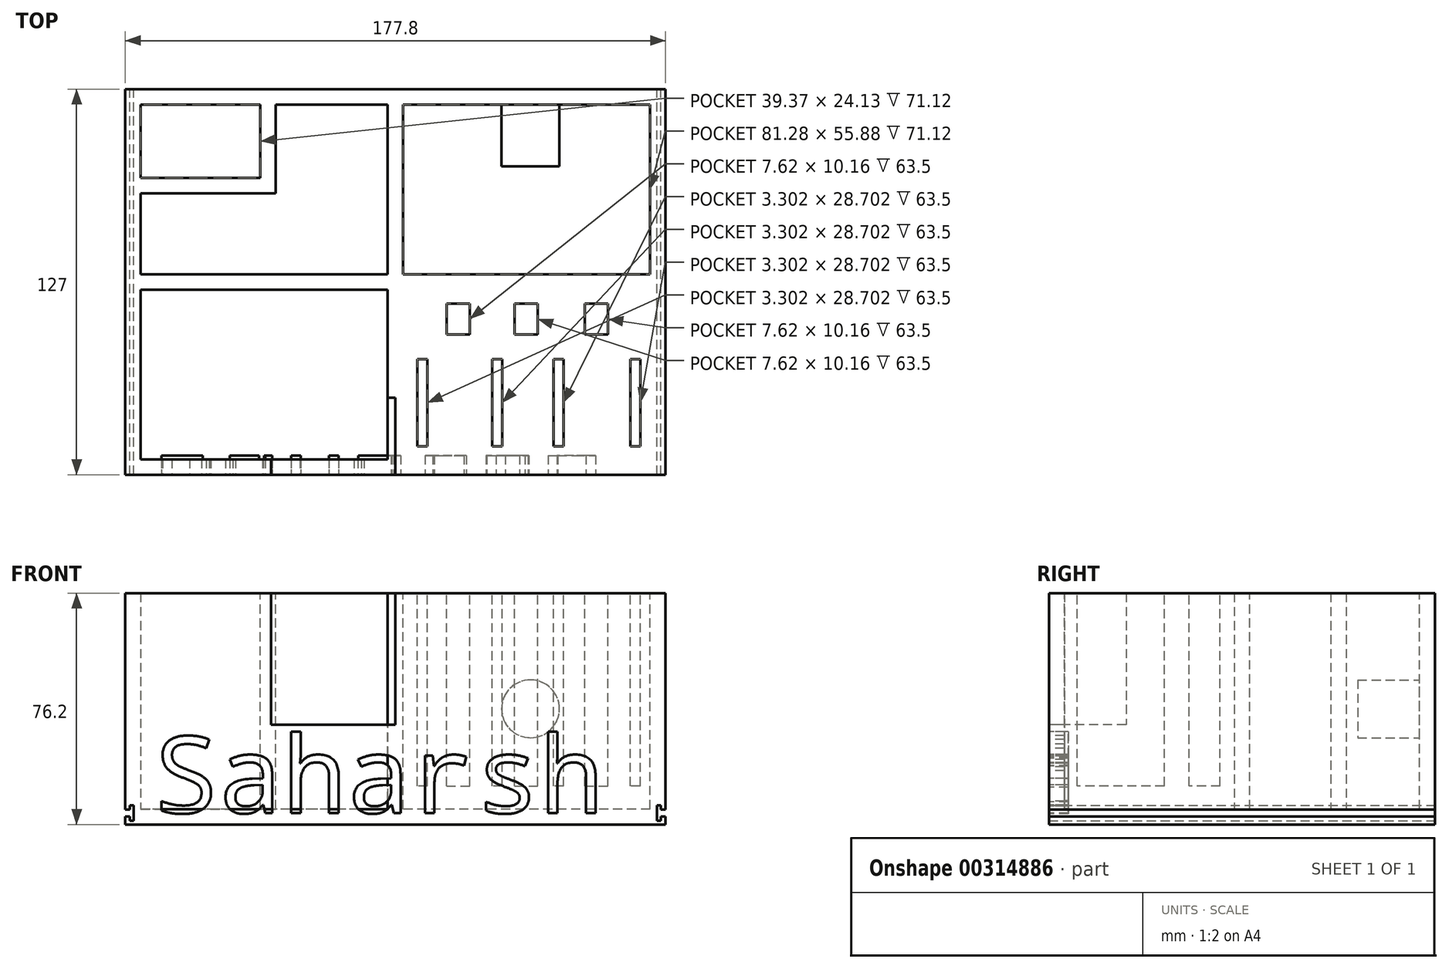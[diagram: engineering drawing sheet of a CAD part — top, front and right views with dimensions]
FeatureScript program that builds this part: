
annotation { "Feature Type Name" : "Feature", "Feature Type Description" : "" }
export const myFeature = defineFeature(function(context is Context, id is Id, definition is map)
    precondition{}
    {
        {
            var Q0;
            Q0=qCreatedBy(makeId("Top.planeOp"),FACE);
            var sketch = newSketch(context, id + "F0", { "sketchPlane" : qUnion([Q0])});
            skLineSegment(sketch, "E0.bottom", {"start": v(88.9, 63.5) * mm, "end": v(-88.9, 63.5) * mm});
            skLineSegment(sketch, "E0.top", {"start": v(88.9, -63.5) * mm, "end": v(-88.9, -63.5) * mm});
            skLineSegment(sketch, "E0.left", {"start": v(88.9, 63.5) * mm, "end": v(88.9, -63.5) * mm});
            skLineSegment(sketch, "E0.right", {"start": v(-88.9, 63.5) * mm, "end": v(-88.9, -63.5) * mm});
            skPoint(sketch, "E0.middle", {"position": v(0, 0) * mm});
            skSolve(sketch);
        }
        {
            var Q0;
            Q0 = qSketchRegion(id + "F0", true);
            extrude(context, id + "F1", {"entities" : qUnion([Q0]), "depth" : 76.2 * mm});
        }
        {
            var Q0;
            Q0=makeQuery(id+"F1.opExtrude","CAP_FACE",FACE,{"disambiguationData":[OSD([sQuery(id+"F0.wireOp",EDGE,"E0.bottom"),sQuery(id+"F0.wireOp",EDGE,"E0.top"),sQuery(id+"F0.wireOp",EDGE,"E0.left"),sQuery(id+"F0.wireOp",EDGE,"E0.right")])],"isStart":false});
            var sketch = newSketch(context, id + "F2", { "sketchPlane" : qUnion([Q0])});
            skLineSegment(sketch, "E1.bottom", {"start": v(-88.9, 63.5) * mm, "end": v(0, 63.5) * mm});
            skLineSegment(sketch, "E1.top", {"start": v(-88.9, 0) * mm, "end": v(0, 0) * mm});
            skLineSegment(sketch, "E1.left", {"start": v(-88.9, 63.5) * mm, "end": v(-88.9, 0) * mm});
            skLineSegment(sketch, "E1.right", {"start": v(0, 63.5) * mm, "end": v(0, 0) * mm});
            skLineSegment(sketch, "E2.bottom", {"start": v(0, 0) * mm, "end": v(88.9, 0) * mm});
            skLineSegment(sketch, "E2.top", {"start": v(0, 63.5) * mm, "end": v(88.9, 63.5) * mm});
            skLineSegment(sketch, "E2.left", {"start": v(0, 0) * mm, "end": v(0, 63.5) * mm});
            skLineSegment(sketch, "E2.right", {"start": v(88.9, 0) * mm, "end": v(88.9, 63.5) * mm});
            skLineSegment(sketch, "E3.top", {"start": v(0, -63.5) * mm, "end": v(88.9, -63.5) * mm});
            skLineSegment(sketch, "E3.left", {"start": v(0, 0) * mm, "end": v(0, -63.5) * mm});
            skLineSegment(sketch, "E3.right", {"start": v(88.9, 0) * mm, "end": v(88.9, -63.5) * mm});
            skLineSegment(sketch, "E4.bottom", {"start": v(0, 0) * mm, "end": v(-88.9, 0) * mm});
            skLineSegment(sketch, "E4.top", {"start": v(0, -63.5) * mm, "end": v(-88.9, -63.5) * mm});
            skLineSegment(sketch, "E4.right", {"start": v(-88.9, 0) * mm, "end": v(-88.9, -63.5) * mm});
            skSolve(sketch);
        }
        {
            var Q0;
            Q0=makeQuery(id+"F1.opExtrude","CAP_FACE",FACE,{"disambiguationData":[OSD([sQuery(id+"F0.wireOp",EDGE,"E0.bottom"),sQuery(id+"F0.wireOp",EDGE,"E0.top"),sQuery(id+"F0.wireOp",EDGE,"E0.left"),sQuery(id+"F0.wireOp",EDGE,"E0.right")])],"isStart":false});
            shell(context, id + "F3", {"entities" : qUnion([Q0]), "thickness" : 5.08 * mm});
        }
        {
            var Q0;
            Q0=qCreatedBy(makeId("Top.planeOp"),FACE);
            var sketch = newSketch(context, id + "F4", { "sketchPlane" : qUnion([Q0])});
            skLineSegment(sketch, "E5.bottom", {"start": v(-2.54, 63.5) * mm, "end": v(2.54, 63.5) * mm});
            skLineSegment(sketch, "E5.top", {"start": v(-2.54, -63.5) * mm, "end": v(2.54, -63.5) * mm});
            skLineSegment(sketch, "E5.left", {"start": v(-2.54, 63.5) * mm, "end": v(-2.54, -63.5) * mm});
            skLineSegment(sketch, "E5.right", {"start": v(2.54, 63.5) * mm, "end": v(2.54, -63.5) * mm});
            skPoint(sketch, "E6", {"position": v(0, 63.5) * mm});
            skPoint(sketch, "E7", {"position": v(0, -63.5) * mm});
            skLineSegment(sketch, "E8.bottom", {"start": v(-88.9, 2.54) * mm, "end": v(88.9, 2.54) * mm});
            skLineSegment(sketch, "E8.top", {"start": v(-88.9, -2.54) * mm, "end": v(88.9, -2.54) * mm});
            skLineSegment(sketch, "E8.left", {"start": v(-88.9, 2.54) * mm, "end": v(-88.9, -2.54) * mm});
            skLineSegment(sketch, "E8.right", {"start": v(88.9, 2.54) * mm, "end": v(88.9, -2.54) * mm});
            skPoint(sketch, "E9", {"position": v(-88.9, 0) * mm});
            skPoint(sketch, "E10", {"position": v(88.9, 0) * mm});
            skSolve(sketch);
        }
        {
            var Q0;
            Q0 = qSketchRegion(id + "F4", true);
            extrude(context, id + "F5", {"entities" : qUnion([Q0]), "operationType" : NewBodyOperationType.ADD, "depth" : 25.4 * mm});
        }
        {
            var Q0;
            Q0 = qSketchRegion(id + "F4", true);
            extrude(context, id + "F6", {"entities" : qUnion([Q0]), "operationType" : NewBodyOperationType.ADD, "depth" : 76.2 * mm});
        }
        {
            var Q0;
            Q0=makeQuery(id+"F2.imprint","IMPRINT",FACE,{"disambiguationData":[TD([[makeQuery(id+"F2.imprint","IMPRINT",EDGE,{"derivedFrom":sQuery(id+"F2.wireOp",EDGE,"E1.bottom")}),1.0]])]});
            var sketch = newSketch(context, id + "F7", { "sketchPlane" : qUnion([Q0])});
            skLineSegment(sketch, "E11.bottom", {"start": v(-88.9, 34.3) * mm, "end": v(-44.45, 34.3) * mm});
            skLineSegment(sketch, "E11.top", {"start": v(-88.9, 29.21) * mm, "end": v(-44.45, 29.21) * mm});
            skLineSegment(sketch, "E11.left", {"start": v(-88.9, 34.29) * mm, "end": v(-88.9, 29.21) * mm});
            skLineSegment(sketch, "E11.right", {"start": v(-44.45, 34.29) * mm, "end": v(-44.45, 29.21) * mm});
            skPoint(sketch, "E12", {"position": v(-88.9, 31.75) * mm});
            skLineSegment(sketch, "E13.bottom", {"start": v(-44.45, 29.21) * mm, "end": v(-39.37, 29.21) * mm});
            skLineSegment(sketch, "E13.top", {"start": v(-44.45, 63.5) * mm, "end": v(-39.37, 63.5) * mm});
            skLineSegment(sketch, "E13.left", {"start": v(-44.45, 29.21) * mm, "end": v(-44.45, 63.5) * mm});
            skLineSegment(sketch, "E13.right", {"start": v(-39.37, 29.21) * mm, "end": v(-39.37, 63.5) * mm});
            skSolve(sketch);
        }
        {
            var Q0;
            Q0 = qSketchRegion(id + "F7", true);
            extrude(context, id + "F8", {"entities" : qUnion([Q0]), "operationType" : NewBodyOperationType.ADD, "oppositeDirection" : true, "depth" : 76.2 * mm});
        }
        {
            var Q0;
            Q0=makeQuery(id+"F1.opExtrude","SWEPT_FACE",FACE,{"disambiguationData":[OSD([sQuery(id+"F0.wireOp",EDGE,"E0.bottom")])]});
            var sketch = newSketch(context, id + "F9", { "sketchPlane" : qUnion([Q0])});
            skCircle(sketch, "E14", {"center": v(-44.45, 38.1) * mm, "radius": 9.53 * mm});
            skPoint(sketch, "E15", {"position": v(-88.9, 38.1) * mm});
            skSolve(sketch);
        }
        {
            var Q0;
            Q0 = qSketchRegion(id + "F9", true);
            extrude(context, id + "F10", {"entities" : qUnion([Q0]), "operationType" : NewBodyOperationType.ADD, "oppositeDirection" : true, "depth" : 25.4 * mm});
        }
        {
            var Q0;
            Q0=makeQuery(id+"F1.opExtrude","SWEPT_FACE",FACE,{"disambiguationData":[OSD([sQuery(id+"F0.wireOp",EDGE,"E0.top")])]});
            var sketch = newSketch(context, id + "F11", { "sketchPlane" : qUnion([Q0])});
            skLineSegment(sketch, "E16.bottom", {"start": v(0, 32.88) * mm, "end": v(-40.92, 32.88) * mm});
            skLineSegment(sketch, "E16.top", {"start": v(0, 76.2) * mm, "end": v(-40.92, 76.2) * mm});
            skLineSegment(sketch, "E16.left", {"start": v(0, 32.88) * mm, "end": v(0, 76.2) * mm});
            skLineSegment(sketch, "E16.right", {"start": v(-40.92, 32.88) * mm, "end": v(-40.92, 76.2) * mm});
            skSolve(sketch);
        }
        {
            var Q0;
            Q0 = qSketchRegion(id + "F11", true);
            extrude(context, id + "F12", {"entities" : qUnion([Q0]), "operationType" : NewBodyOperationType.REMOVE, "oppositeDirection" : true, "depth" : 25.4 * mm});
        }
        {
            var Q0;
            Q0=qCreatedBy(makeId("Top.planeOp"),FACE);
            var sketch = newSketch(context, id + "F13", { "sketchPlane" : qUnion([Q0])});
            skLineSegment(sketch, "E17.bottom", {"start": v(0, 0) * mm, "end": v(87.76, 0) * mm});
            skLineSegment(sketch, "E17.top", {"start": v(0, -60.6) * mm, "end": v(87.76, -60.6) * mm});
            skLineSegment(sketch, "E17.left", {"start": v(0, 0) * mm, "end": v(0, -60.6) * mm});
            skLineSegment(sketch, "E17.right", {"start": v(87.76, 0) * mm, "end": v(87.76, -60.6) * mm});
            skSolve(sketch);
        }
        {
            var Q0;
            Q0 = qSketchRegion(id + "F13", true);
            extrude(context, id + "F14", {"entities" : qUnion([Q0]), "operationType" : NewBodyOperationType.ADD, "depth" : 76.2 * mm});
        }
        {
            var Q0;
            Q0=makeQuery(id+"F2.imprint","IMPRINT",FACE,{"disambiguationData":[TD([[makeQuery(id+"F2.imprint","IMPRINT",EDGE,{"derivedFrom":sQuery(id+"F2.wireOp",EDGE,"E2.bottom")}),-1.0]])]});
            var sketch = newSketch(context, id + "F15", { "sketchPlane" : qUnion([Q0])});
            skLineSegment(sketch, "E18.bottom", {"start": v(16.83, -7.17) * mm, "end": v(24.45, -7.17) * mm});
            skLineSegment(sketch, "E18.top", {"start": v(16.83, -17.33) * mm, "end": v(24.45, -17.33) * mm});
            skLineSegment(sketch, "E18.left", {"start": v(16.83, -7.17) * mm, "end": v(16.83, -17.33) * mm});
            skLineSegment(sketch, "E18.right", {"start": v(24.45, -7.17) * mm, "end": v(24.45, -17.33) * mm});
            skLineSegment(sketch, "E19.bottom", {"start": v(10.56, -25.52) * mm, "end": v(7.26, -25.52) * mm});
            skLineSegment(sketch, "E19.top", {"start": v(10.56, -54.22) * mm, "end": v(7.26, -54.22) * mm});
            skLineSegment(sketch, "E19.left", {"start": v(10.56, -25.52) * mm, "end": v(10.56, -54.22) * mm});
            skLineSegment(sketch, "E19.right", {"start": v(7.26, -25.52) * mm, "end": v(7.26, -54.22) * mm});
            skLineSegment(sketch, "E20.bottom", {"start": v(80.56, -25.52) * mm, "end": v(77.26, -25.52) * mm});
            skLineSegment(sketch, "E20.top", {"start": v(80.56, -54.22) * mm, "end": v(77.26, -54.22) * mm});
            skLineSegment(sketch, "E20.left", {"start": v(80.56, -25.52) * mm, "end": v(80.56, -54.22) * mm});
            skLineSegment(sketch, "E20.right", {"start": v(77.26, -25.52) * mm, "end": v(77.26, -54.22) * mm});
            skLineSegment(sketch, "E21.bottom", {"start": v(35.2, -25.52) * mm, "end": v(31.9, -25.52) * mm});
            skLineSegment(sketch, "E21.top", {"start": v(35.2, -54.22) * mm, "end": v(31.9, -54.22) * mm});
            skLineSegment(sketch, "E21.left", {"start": v(35.2, -25.52) * mm, "end": v(35.2, -54.22) * mm});
            skLineSegment(sketch, "E21.right", {"start": v(31.9, -25.52) * mm, "end": v(31.9, -54.22) * mm});
            skLineSegment(sketch, "E22.bottom", {"start": v(55.4, -25.52) * mm, "end": v(52.09, -25.52) * mm});
            skLineSegment(sketch, "E22.top", {"start": v(55.4, -54.22) * mm, "end": v(52.09, -54.22) * mm});
            skLineSegment(sketch, "E22.left", {"start": v(55.4, -25.52) * mm, "end": v(55.4, -54.22) * mm});
            skLineSegment(sketch, "E22.right", {"start": v(52.09, -25.52) * mm, "end": v(52.09, -54.22) * mm});
            skLineSegment(sketch, "E23.bottom", {"start": v(62.3, -7.17) * mm, "end": v(69.92, -7.17) * mm});
            skLineSegment(sketch, "E23.top", {"start": v(62.3, -17.33) * mm, "end": v(69.92, -17.33) * mm});
            skLineSegment(sketch, "E23.left", {"start": v(62.3, -7.17) * mm, "end": v(62.3, -17.33) * mm});
            skLineSegment(sketch, "E23.right", {"start": v(69.92, -7.17) * mm, "end": v(69.92, -17.33) * mm});
            skLineSegment(sketch, "E24.bottom", {"start": v(39.26, -7.17) * mm, "end": v(46.88, -7.17) * mm});
            skLineSegment(sketch, "E24.top", {"start": v(39.26, -17.33) * mm, "end": v(46.88, -17.33) * mm});
            skLineSegment(sketch, "E24.left", {"start": v(39.26, -7.17) * mm, "end": v(39.26, -17.33) * mm});
            skLineSegment(sketch, "E24.right", {"start": v(46.88, -7.17) * mm, "end": v(46.88, -17.33) * mm});
            skSolve(sketch);
        }
        {
            var Q0;
            Q0 = qSketchRegion(id + "F15", true);
            extrude(context, id + "F16", {"entities" : qUnion([Q0]), "operationType" : NewBodyOperationType.REMOVE, "oppositeDirection" : true, "depth" : 63.5 * mm});
        }
        {
            var Q0;
            Q0=makeQuery(id+"F1.opExtrude","SWEPT_FACE",FACE,{"disambiguationData":[OSD([sQuery(id+"F0.wireOp",EDGE,"E0.bottom")])]});
            var sketch = newSketch(context, id + "F17", { "sketchPlane" : qUnion([Q0])});
            skLineSegment(sketch, "E25.MirrorCS", {"start": v(87.37, 4.95) * mm, "end": v(87.37, 2.67) * mm});
            skPoint(sketch, "E26.MirrorP", {"position": v(87.37, 3.81) * mm});
            skLineSegment(sketch, "E27.MirrorCS", {"start": v(87.37, 6.35) * mm, "end": v(87.37, 1.27) * mm});
            skLineSegment(sketch, "E28.MirrorCS", {"start": v(86.1, 6.35) * mm, "end": v(86.1, 1.27) * mm});
            skLineSegment(sketch, "E29.MirrorCS", {"start": v(88.9, 4.95) * mm, "end": v(87.37, 4.95) * mm});
            skLineSegment(sketch, "E30.MirrorCS", {"start": v(87.37, 1.27) * mm, "end": v(86.1, 1.27) * mm});
            skLineSegment(sketch, "E31.MirrorCS", {"start": v(88.9, 2.67) * mm, "end": v(87.37, 2.67) * mm});
            skLineSegment(sketch, "E32.MirrorCS", {"start": v(88.9, 4.95) * mm, "end": v(88.9, 2.67) * mm});
            skLineSegment(sketch, "E33.MirrorCS", {"start": v(87.37, 6.35) * mm, "end": v(86.1, 6.35) * mm});
            skLineSegment(sketch, "E34", {"start": v(88.9, 0) * mm, "end": v(88.9, 3.81) * mm});
            skPoint(sketch, "E35", {"position": v(88.9, 3.81) * mm});
            skLineSegment(sketch, "E36.MirrorCS", {"start": v(-87.37, 1.27) * mm, "end": v(-86.1, 1.27) * mm});
            skLineSegment(sketch, "E37.MirrorCS", {"start": v(-88.9, 2.67) * mm, "end": v(-87.37, 2.67) * mm});
            skLineSegment(sketch, "E38.MirrorCS", {"start": v(-87.37, 4.95) * mm, "end": v(-87.37, 2.67) * mm});
            skLineSegment(sketch, "E39.MirrorCS", {"start": v(-88.9, 4.95) * mm, "end": v(-88.9, 2.67) * mm});
            skLineSegment(sketch, "E40.MirrorCS", {"start": v(-87.37, 6.35) * mm, "end": v(-87.37, 1.27) * mm});
            skLineSegment(sketch, "E41.MirrorCS", {"start": v(-88.9, 4.95) * mm, "end": v(-87.37, 4.95) * mm});
            skLineSegment(sketch, "E42.MirrorCS", {"start": v(-87.37, 6.35) * mm, "end": v(-86.1, 6.35) * mm});
            skPoint(sketch, "E43.MirrorP", {"position": v(-87.37, 3.81) * mm});
            skLineSegment(sketch, "E44.MirrorCS", {"start": v(-86.1, 6.35) * mm, "end": v(-86.1, 1.27) * mm});
            skPoint(sketch, "E45.MirrorP", {"position": v(-88.9, 3.81) * mm});
            skLineSegment(sketch, "E46.MirrorCS", {"start": v(-88.9, 0) * mm, "end": v(-88.9, 3.81) * mm});
            skLineSegment(sketch, "E47", {"start": v(-88.9, 2.67) * mm, "end": v(-88.9, 0) * mm});
            skSolve(sketch);
        }
        {
            var Q0;
            Q0 = qSketchRegion(id + "F17", true);
            extrude(context, id + "F18", {"entities" : qUnion([Q0]), "operationType" : NewBodyOperationType.REMOVE, "oppositeDirection" : true, "depth" : 127 * mm});
        }
        {
            var Q0;
            Q0=makeQuery(id+"F1.opExtrude","SWEPT_FACE",FACE,{"disambiguationData":[OSD([sQuery(id+"F0.wireOp",EDGE,"E0.top")])]});
            var sketch = newSketch(context, id + "F19", { "sketchPlane" : qUnion([Q0])});
            skText(sketch, "E48", { "text": "Saharsh", "fontName": "DroidSansMono.ttf"});
            skPoint(sketch, "E48.secondSnap0", {"position": v(86.1, 3.8) * mm});
            const initialGuessF19  = {"E48": [-0.07938, 0.0038, 1, 0, 0.02536]};
            skSetInitialGuess(sketch, initialGuessF19);
            skSolve(sketch);
        }
        {
            var Q0;
            Q0 = qSketchRegion(id + "F19", true);
            extrude(context, id + "F20", {"entities" : qUnion([Q0]), "operationType" : NewBodyOperationType.REMOVE, "oppositeDirection" : true, "depth" : 6.35 * mm});
        }
    });
